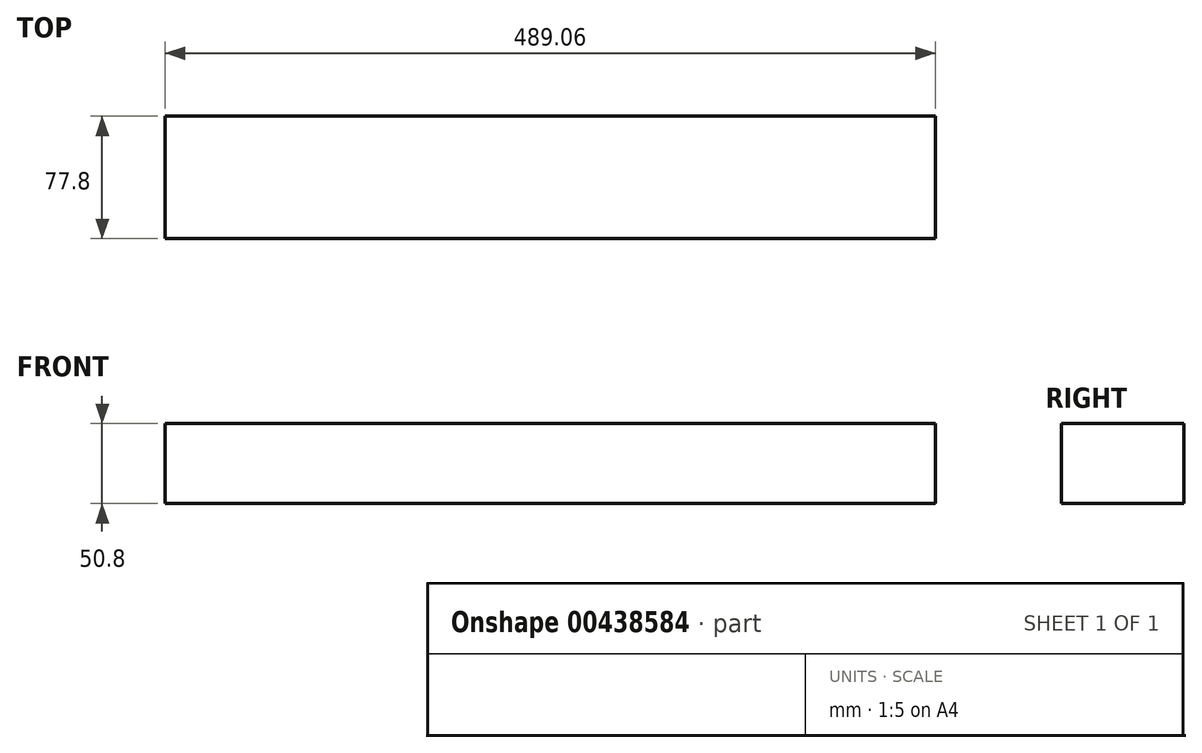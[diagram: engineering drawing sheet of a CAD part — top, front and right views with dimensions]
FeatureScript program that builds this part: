
annotation { "Feature Type Name" : "Feature", "Feature Type Description" : "" }
export const myFeature = defineFeature(function(context is Context, id is Id, definition is map)
    precondition{}
    {
        {
            var Q0;
            Q0=qCreatedBy(makeId("Top.planeOp"),FACE);
            var sketch = newSketch(context, id + "F0", { "sketchPlane" : qUnion([Q0])});
            skLineSegment(sketch, "E0.bottom", {"start": v(-244.53, -38.9) * mm, "end": v(244.53, -38.9) * mm});
            skLineSegment(sketch, "E0.top", {"start": v(-244.53, 38.9) * mm, "end": v(244.53, 38.9) * mm});
            skLineSegment(sketch, "E0.left", {"start": v(-244.53, -38.9) * mm, "end": v(-244.53, 38.9) * mm});
            skLineSegment(sketch, "E0.right", {"start": v(244.53, -38.9) * mm, "end": v(244.53, 38.9) * mm});
            skPoint(sketch, "E0.middle", {"position": v(0, 0) * mm});
            skSolve(sketch);
        }
        {
            var Q0;
            Q0 = qSketchRegion(id + "FTy4gaV2v5QadXF_1", true);
            var Q1;
            Q1=makeQuery(id+"F0.imprint","IMPRINT",FACE,{"disambiguationData":[TD([[makeQuery(id+"F0.imprint","IMPRINT",EDGE,{"derivedFrom":sQuery(id+"F0.wireOp",EDGE,"E0.bottom")}),1.0]])]});
            extrude(context, id + "F1", {"entities" : qUnion([Q0, Q1]), "depth" : 50.8 * mm});
        }
    });
